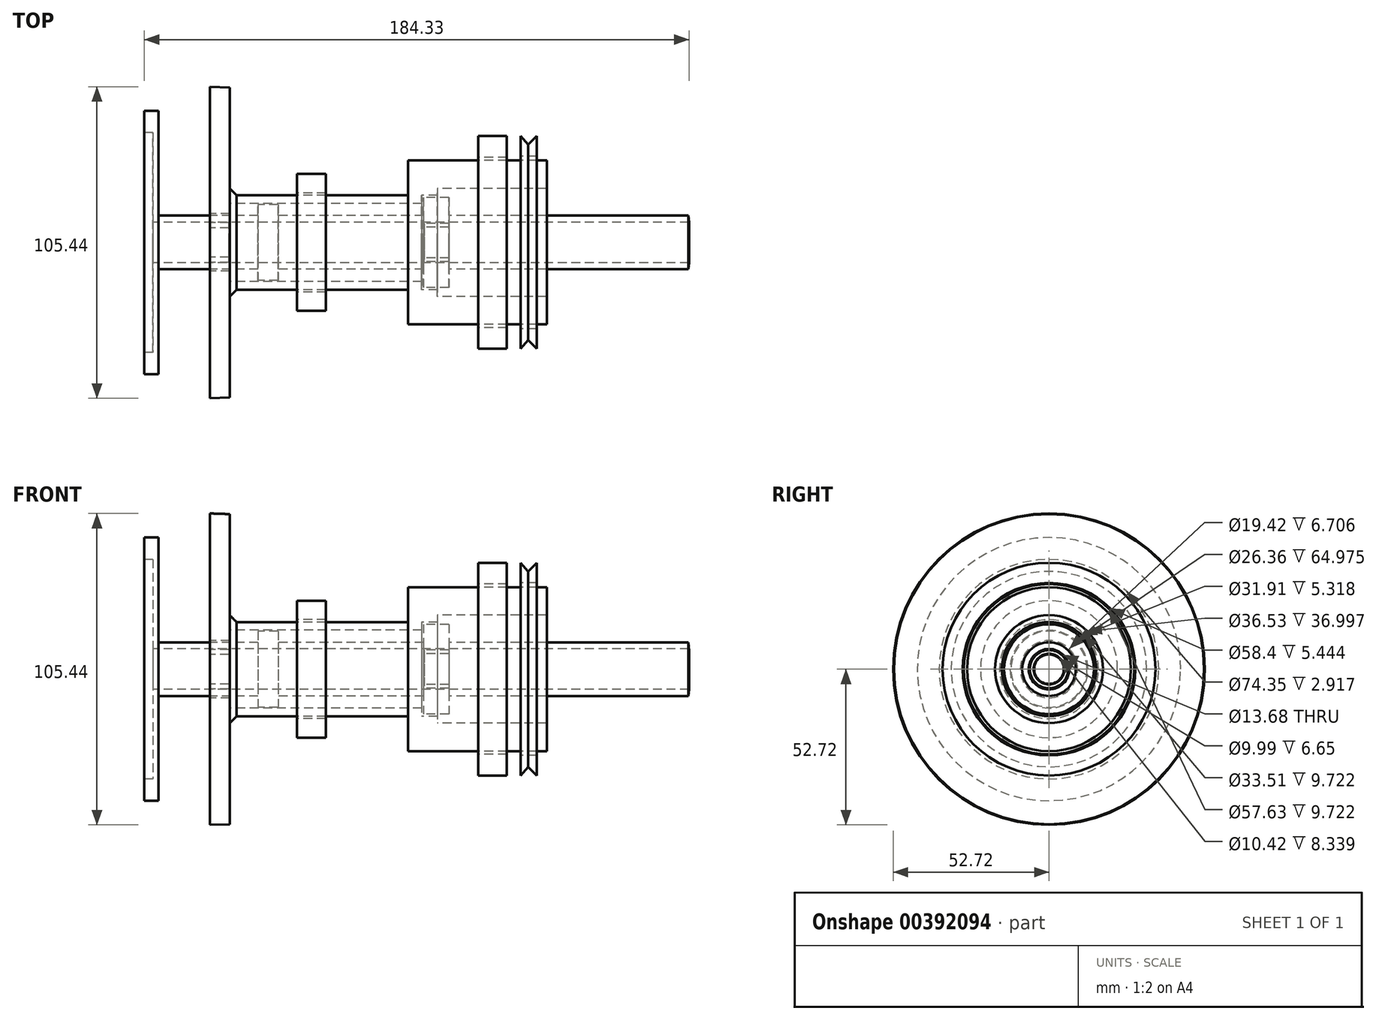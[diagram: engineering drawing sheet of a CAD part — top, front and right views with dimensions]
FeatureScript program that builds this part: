
annotation { "Feature Type Name" : "Feature", "Feature Type Description" : "" }
export const myFeature = defineFeature(function(context is Context, id is Id, definition is map)
    precondition{}
    {
        {
            var Q0;
            Q0=qCreatedBy(makeId("Front.planeOp"),FACE);
            var sketch = newSketch(context, id + "F0", { "sketchPlane" : qUnion([Q0])});
            skLineSegment(sketch, "E0", {"start": v(-51.1, 52.72) * mm, "end": v(-51.1, 9.71) * mm});
            skLineSegment(sketch, "E1", {"start": v(-51.1, 9.71) * mm, "end": v(-44.4, 9.71) * mm});
            skLineSegment(sketch, "E2", {"start": v(-44.4, 9.71) * mm, "end": v(-44.4, 13.18) * mm});
            skLineSegment(sketch, "E3", {"start": v(-44.4, 13.18) * mm, "end": v(20.58, 13.18) * mm});
            skLineSegment(sketch, "E4", {"start": v(20.58, 13.18) * mm, "end": v(20.58, 15.95) * mm});
            skLineSegment(sketch, "E5", {"start": v(20.58, 15.95) * mm, "end": v(25.9, 15.95) * mm});
            skLineSegment(sketch, "E6", {"start": v(25.9, 15.95) * mm, "end": v(25.9, 18.27) * mm});
            skLineSegment(sketch, "E7", {"start": v(25.9, 18.27) * mm, "end": v(62.9, 18.27) * mm});
            skLineSegment(sketch, "E8", {"start": v(62.9, 18.27) * mm, "end": v(62.9, 27.75) * mm});
            skLineSegment(sketch, "E9", {"start": v(62.9, 27.75) * mm, "end": v(15.95, 27.75) * mm});
            skLineSegment(sketch, "E10", {"start": v(15.95, 27.75) * mm, "end": v(15.95, 15.95) * mm});
            skLineSegment(sketch, "E11", {"start": v(15.95, 15.95) * mm, "end": v(10.4, 15.95) * mm});
            skLineSegment(sketch, "E12", {"start": v(10.4, 15.95) * mm, "end": v(-42.08, 15.95) * mm});
            skLineSegment(sketch, "E13", {"start": v(-44.4, 18.27) * mm, "end": v(-44.4, 52.49) * mm});
            skLineSegment(sketch, "E14", {"start": v(-44.4, 52.49) * mm, "end": v(-51.1, 52.72) * mm});
            skLineSegment(sketch, "E15", {"start": v(-44.4, 18.27) * mm, "end": v(-42.08, 15.95) * mm});
            skSolve(sketch);
        }
        {
            var Q0;
            Q0=qCreatedBy(makeId("Front.planeOp"),FACE);
            var sketch = newSketch(context, id + "F1", { "sketchPlane" : qUnion([Q0])});
            skLineSegment(sketch, "E16", {"start": v(-127.85, 4.65) * mm, "end": v(156, 4.65) * mm});
            skLineSegment(sketch, "E17.bottom", {"start": v(156, 4.65) * mm, "end": v(76.2, 4.65) * mm});
            skLineSegment(sketch, "E17.top", {"start": v(156, 0) * mm, "end": v(76.2, 0) * mm});
            skLineSegment(sketch, "E17.left", {"start": v(156, 4.65) * mm, "end": v(156, 0) * mm});
            skLineSegment(sketch, "E17.right", {"start": v(76.2, 4.65) * mm, "end": v(76.2, 0) * mm});
            skLineSegment(sketch, "E18.bottom", {"start": v(-127.85, 4.65) * mm, "end": v(-76.84, 4.65) * mm});
            skLineSegment(sketch, "E18.top", {"start": v(-127.85, 0) * mm, "end": v(-76.84, 0) * mm});
            skLineSegment(sketch, "E18.left", {"start": v(-127.85, 4.65) * mm, "end": v(-127.85, 0) * mm});
            skLineSegment(sketch, "E18.right", {"start": v(-76.84, 4.65) * mm, "end": v(-76.84, 0) * mm});
            skSolve(sketch);
        }
        {
            var Q0;
            Q0=qCreatedBy(makeId("Front.planeOp"),FACE);
            var sketch = newSketch(context, id + "F2", { "sketchPlane" : qUnion([Q0])});
            skLineSegment(sketch, "E19.bottom", {"start": v(-34.8, 12.87) * mm, "end": v(-28, 12.87) * mm});
            skLineSegment(sketch, "E19.left", {"start": v(-34.8, 12.87) * mm, "end": v(-34.8, 9.08) * mm});
            skLineSegment(sketch, "E19.right", {"start": v(-28, 12.87) * mm, "end": v(-28, 9.08) * mm});
            skLineSegment(sketch, "E20.bottom", {"start": v(21.2, 15.2) * mm, "end": v(29.75, 15.2) * mm});
            skLineSegment(sketch, "E20.left", {"start": v(21.2, 15.2) * mm, "end": v(21.2, 9.08) * mm});
            skLineSegment(sketch, "E20.right", {"start": v(29.75, 15.2) * mm, "end": v(29.75, 9.08) * mm});
            skLineSegment(sketch, "E21.bottom", {"start": v(-21.58, 23.17) * mm, "end": v(-11.86, 23.17) * mm});
            skLineSegment(sketch, "E21.top", {"start": v(-21.58, 16.76) * mm, "end": v(-11.86, 16.76) * mm});
            skLineSegment(sketch, "E21.left", {"start": v(-21.58, 23.17) * mm, "end": v(-21.58, 16.76) * mm});
            skLineSegment(sketch, "E21.right", {"start": v(-11.86, 23.17) * mm, "end": v(-11.86, 16.76) * mm});
            skLineSegment(sketch, "E22.bottom", {"start": v(39.67, 36) * mm, "end": v(49.39, 36) * mm});
            skLineSegment(sketch, "E22.top", {"start": v(39.67, 28.81) * mm, "end": v(49.39, 28.81) * mm});
            skLineSegment(sketch, "E22.left", {"start": v(39.67, 36) * mm, "end": v(39.67, 28.81) * mm});
            skLineSegment(sketch, "E22.right", {"start": v(49.39, 36) * mm, "end": v(49.39, 28.81) * mm});
            skLineSegment(sketch, "E23", {"start": v(54.06, 36) * mm, "end": v(54.06, 29.2) * mm});
            skLineSegment(sketch, "E24", {"start": v(54.06, 29.2) * mm, "end": v(59.5, 29.2) * mm});
            skLineSegment(sketch, "E25", {"start": v(59.5, 29.2) * mm, "end": v(59.5, 36) * mm});
            skLineSegment(sketch, "E26", {"start": v(59.5, 36) * mm, "end": v(56.58, 33.1) * mm});
            skLineSegment(sketch, "E27", {"start": v(56.58, 33.1) * mm, "end": v(54.06, 36) * mm});
            skLineSegment(sketch, "E28", {"start": v(-68.44, 9.08) * mm, "end": v(110.83, 9.08) * mm});
            skPoint(sketch, "E28.startSnap0", {"position": v(-34.8, 9.08) * mm});
            skLineSegment(sketch, "E29", {"start": v(-68.44, 9.08) * mm, "end": v(-68.44, 44.56) * mm});
            skLineSegment(sketch, "E30", {"start": v(-68.44, 44.56) * mm, "end": v(-73.3, 44.56) * mm});
            skLineSegment(sketch, "E31", {"start": v(-73.3, 44.56) * mm, "end": v(-73.3, 37.17) * mm});
            skLineSegment(sketch, "E32", {"start": v(-73.3, 37.17) * mm, "end": v(-70.39, 37.17) * mm});
            skLineSegment(sketch, "E33", {"start": v(-70.39, 37.17) * mm, "end": v(-70.39, 6.84) * mm});
            skLineSegment(sketch, "E34", {"start": v(-70.39, 6.84) * mm, "end": v(111.03, 6.84) * mm});
            skLineSegment(sketch, "E35", {"start": v(111.03, 6.84) * mm, "end": v(110.83, 9.08) * mm});
            skLineSegment(sketch, "E36.MirrorCS", {"start": v(66.11, 9.08) * mm, "end": v(66.11, 36) * mm});
            skLineSegment(sketch, "E37.MirrorCS", {"start": v(71.55, 29.2) * mm, "end": v(66.11, 29.2) * mm});
            skLineSegment(sketch, "E38.MirrorCS", {"start": v(69.03, 33.1) * mm, "end": v(71.55, 36) * mm});
            skLineSegment(sketch, "E39.MirrorCS", {"start": v(66.11, 36) * mm, "end": v(69.03, 33.1) * mm});
            skSolve(sketch);
        }
        {
            var Q0;
            Q0=qCreatedBy(makeId("Front.planeOp"),FACE);
            var sketch = newSketch(context, id + "F3", { "sketchPlane" : qUnion([Q0])});
            skLineSegment(sketch, "E40.bottom", {"start": v(-51.28, 6.69) * mm, "end": v(-44.63, 6.69) * mm});
            skLineSegment(sketch, "E40.top", {"start": v(-51.28, 5) * mm, "end": v(-44.63, 5) * mm});
            skLineSegment(sketch, "E40.left", {"start": v(-51.28, 6.69) * mm, "end": v(-51.28, 5) * mm});
            skLineSegment(sketch, "E40.right", {"start": v(-44.63, 6.69) * mm, "end": v(-44.63, 5) * mm});
            skLineSegment(sketch, "E41.bottom", {"start": v(21.45, 6.47) * mm, "end": v(29.79, 6.47) * mm});
            skLineSegment(sketch, "E41.top", {"start": v(21.45, 5.2) * mm, "end": v(29.79, 5.2) * mm});
            skLineSegment(sketch, "E41.left", {"start": v(21.45, 6.47) * mm, "end": v(21.45, 5.2) * mm});
            skLineSegment(sketch, "E41.right", {"start": v(29.79, 6.47) * mm, "end": v(29.79, 5.2) * mm});
            skSolve(sketch);
        }
        {
            var Q0;
            Q0=makeQuery(id+"F0.imprint","IMPRINT",FACE,{"disambiguationData":[TD([[makeQuery(id+"F0.imprint","IMPRINT",EDGE,{"derivedFrom":sQuery(id+"F0.wireOp",EDGE,"E0")}),1.0]])]});
            var Q1;
            Q1=makeQuery(id+"F1.imprint","IMPRINT",FACE,{"disambiguationData":[TD([[makeQuery(id+"F1.imprint","IMPRINT",EDGE,{"derivedFrom":sQuery(id+"F1.wireOp",EDGE,"E18.bottom")}),-1.0]])]});
            var Q2;
            Q2=makeQuery(id+"F1.imprint","IMPRINT",FACE,{"disambiguationData":[TD([[makeQuery(id+"F1.imprint","IMPRINT",EDGE,{"derivedFrom":sQuery(id+"F1.wireOp",EDGE,"E17.bottom")}),1.0]])]});
            var Q3;
            {var subQ0=sQuery(id+"F2.wireOp",EDGE,"E29");Q3=makeQuery(id+"F2.imprint","IMPRINT",FACE,{"disambiguationData":[TD([[makeQuery(id+"F2.imprint","IMPRINT",EDGE,{"derivedFrom":subQ0}),1.0]])]});}
            var Q4;
            Q4=makeQuery(id+"F2.imprint","IMPRINT",FACE,{"disambiguationData":[TD([[makeQuery(id+"F2.imprint","IMPRINT",EDGE,{"derivedFrom":sQuery(id+"F2.wireOp",EDGE,"E22.bottom")}),-1.0]])]});
            var Q5;
            Q5=makeQuery(id+"F2.imprint","IMPRINT",FACE,{"disambiguationData":[TD([[makeQuery(id+"F2.imprint","IMPRINT",EDGE,{"derivedFrom":sQuery(id+"F2.wireOp",EDGE,"E21.bottom")}),-1.0]])]});
            var Q6;
            Q6=makeQuery(id+"F2.imprint","IMPRINT",FACE,{"disambiguationData":[TD([[makeQuery(id+"F2.imprint","IMPRINT",EDGE,{"derivedFrom":sQuery(id+"F2.wireOp",EDGE,"E19.bottom")}),-1.0]])]});
            var Q7;
            Q7=makeQuery(id+"F2.imprint","IMPRINT",FACE,{"disambiguationData":[TD([[makeQuery(id+"F2.imprint","IMPRINT",EDGE,{"derivedFrom":sQuery(id+"F2.wireOp",EDGE,"E20.bottom")}),-1.0]])]});
            var Q8;
            Q8=makeQuery(id+"F3.imprint","IMPRINT",FACE,{"disambiguationData":[TD([[makeQuery(id+"F3.imprint","IMPRINT",EDGE,{"derivedFrom":sQuery(id+"F3.wireOp",EDGE,"E40.bottom")}),-1.0]])]});
            var Q9;
            Q9=makeQuery(id+"F2.imprint","IMPRINT",FACE,{"disambiguationData":[TD([[makeQuery(id+"F2.imprint","IMPRINT",EDGE,{"derivedFrom":sQuery(id+"F2.wireOp",EDGE,"E23")}),1.0]])]});
            var Q10;
            Q10=makeQuery(id+"F3.imprint","IMPRINT",FACE,{"disambiguationData":[TD([[makeQuery(id+"F3.imprint","IMPRINT",EDGE,{"derivedFrom":sQuery(id+"F3.wireOp",EDGE,"E41.bottom")}),-1.0]])]});
            var Q11;
            Q11=sQuery(id+"F1.wireOp",EDGE,"E18.top");
            revolve(context, id + "F4", {"entities" : qUnion([Q0, Q1, Q2, Q3, Q4, Q5, Q6, Q7, Q8, Q9, Q10]), "axis" : qUnion([Q11]), "revolveType" : RevolveType.FULL});
        }
    });
